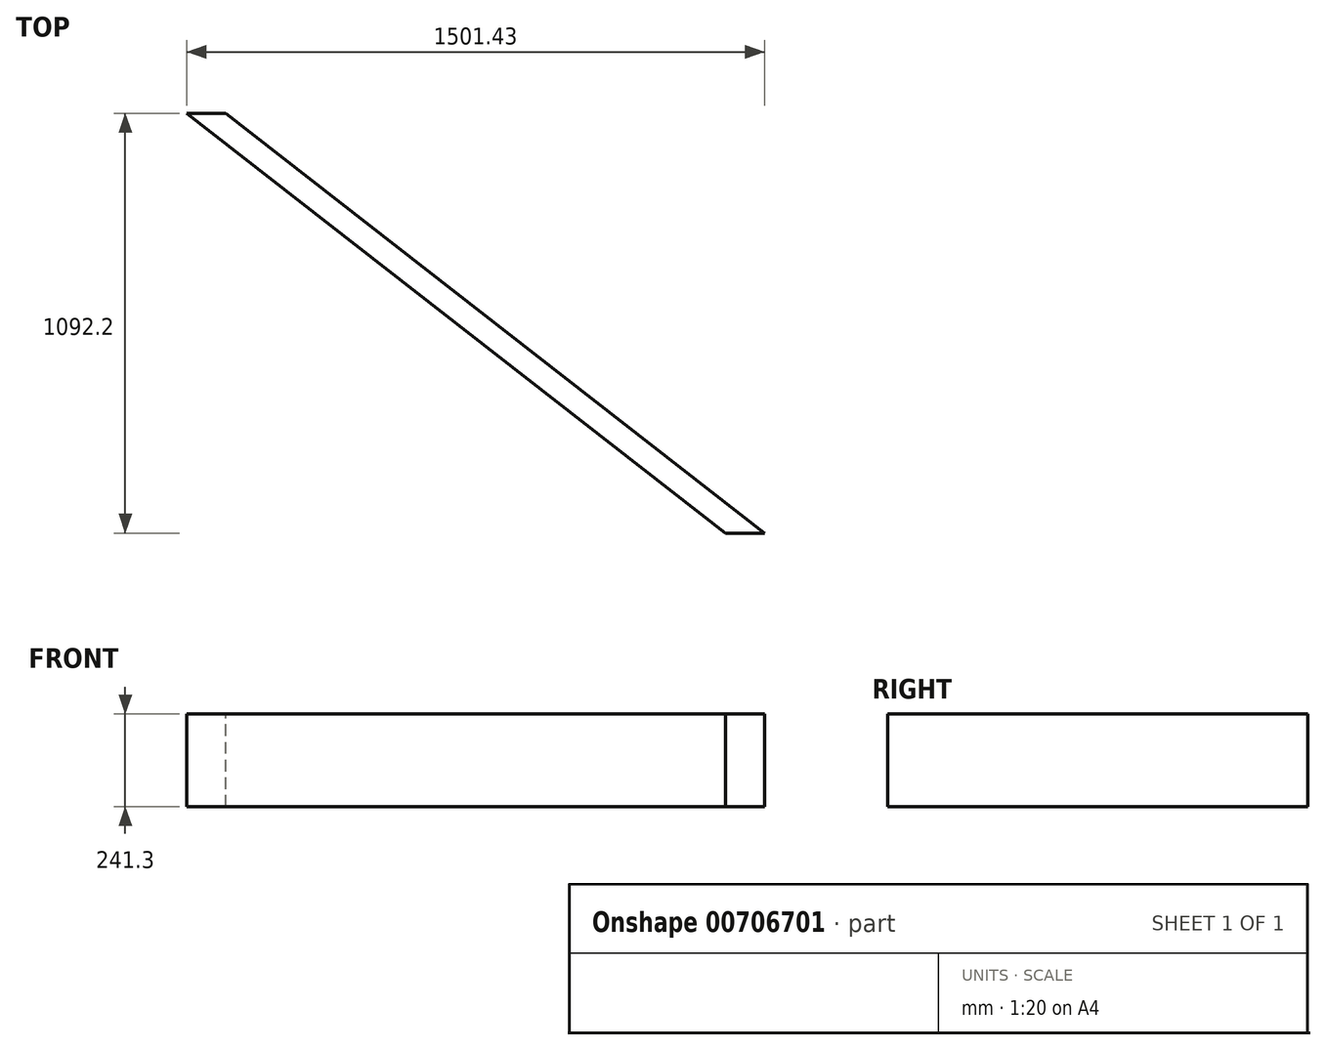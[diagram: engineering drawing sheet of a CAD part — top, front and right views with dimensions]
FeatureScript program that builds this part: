
annotation { "Feature Type Name" : "Feature", "Feature Type Description" : "" }
export const myFeature = defineFeature(function(context is Context, id is Id, definition is map)
    precondition{}
    {
        {
            var Q0;
            Q0=qCreatedBy(makeId("Top.planeOp"),FACE);
            var sketch = newSketch(context, id + "F0", { "sketchPlane" : qUnion([Q0])});
            skLineSegment(sketch, "E0", {"start": v(0, 0) * mm, "end": v(1399.83, -1092.2) * mm});
            skLineSegment(sketch, "E1", {"start": v(1399.83, -1092.2) * mm, "end": v(1501.43, -1092.2) * mm});
            skLineSegment(sketch, "E2", {"start": v(1501.43, -1092.2) * mm, "end": v(1501.43, 0) * mm});
            skLineSegment(sketch, "E3", {"start": v(1501.43, 0) * mm, "end": v(0, 0) * mm});
            skSolve(sketch);
        }
        {
            var Q0;
            Q0=makeQuery(id+"F0.imprint","IMPRINT",FACE,{"disambiguationData":[TD([[makeQuery(id+"F0.imprint","IMPRINT",EDGE,{"derivedFrom":sQuery(id+"F0.wireOp",EDGE,"E0")}),1.0]])]});
            extrude(context, id + "F1", {"entities" : qUnion([Q0]), "depth" : 241.3 * mm, "offsetDistance" : 25.4 * mm});
        }
        {
            var Q0;
            Q0=makeQuery(id+"F1.opExtrude","CAP_FACE",FACE,{"disambiguationData":[OSD([sQuery(id+"F0.wireOp",EDGE,"E0"),sQuery(id+"F0.wireOp",EDGE,"E1"),sQuery(id+"F0.wireOp",EDGE,"E2"),sQuery(id+"F0.wireOp",EDGE,"E3")])],"isStart":false});
            var sketch = newSketch(context, id + "F2", { "sketchPlane" : qUnion([Q0])});
            skLineSegment(sketch, "E4", {"start": v(1501.43, 0) * mm, "end": v(1501.43, -1092.2) * mm});
            skLineSegment(sketch, "E5", {"start": v(1501.43, -1092.2) * mm, "end": v(101.6, 0) * mm});
            skLineSegment(sketch, "E6", {"start": v(101.6, 0) * mm, "end": v(1501.43, 0) * mm});
            skSolve(sketch);
        }
        {
            var Q0;
            Q0=makeQuery(id+"F2.imprint","IMPRINT",FACE,{"disambiguationData":[TD([[makeQuery(id+"F2.imprint","IMPRINT",EDGE,{"derivedFrom":sQuery(id+"F2.wireOp",EDGE,"E4")}),1.0]])]});
            extrude(context, id + "F3", {"entities" : qUnion([Q0]), "operationType" : NewBodyOperationType.REMOVE, "oppositeDirection" : true, "depth" : 241.3 * mm, "offsetDistance" : 25.4 * mm});
        }
        {
            var Q0;
            Q0=makeQuery(id+"F1.opExtrude","SWEPT_FACE",FACE,{"disambiguationData":[OSD([sQuery(id+"F0.wireOp",EDGE,"E0")])]});
            var sketch = newSketch(context, id + "F4", { "sketchPlane" : qUnion([Q0])});
            skLineSegment(sketch, "E7.bottom", {"start": v(0, 0) * mm, "end": v(762, 0) * mm});
            skLineSegment(sketch, "E7.top", {"start": v(0, 50.8) * mm, "end": v(762, 50.8) * mm});
            skLineSegment(sketch, "E7.left", {"start": v(0, 0) * mm, "end": v(0, 50.8) * mm});
            skLineSegment(sketch, "E7.right", {"start": v(762, 0) * mm, "end": v(762, 50.8) * mm});
            skSolve(sketch);
        }
        {
            var Q0;
            {var subQ4=sQuery(id+"F4.wireOp",EDGE,"E7.top");Q0=makeQuery(id+"F4.imprint","IMPRINT",FACE,{"disambiguationData":[TD([[makeQuery(id+"F4.imprint","IMPRINT",EDGE,{"derivedFrom":subQ4}),1.0]])]});}
            var sketch = newSketch(context, id + "F5", { "sketchPlane" : qUnion([Q0])});
            skLineSegment(sketch, "E8.bottom", {"start": v(0, 0) * mm, "end": v(25.4, 0) * mm});
            skLineSegment(sketch, "E8.top", {"start": v(0, 50.8) * mm, "end": v(25.4, 50.8) * mm});
            skLineSegment(sketch, "E8.left", {"start": v(0, 0) * mm, "end": v(0, 50.8) * mm});
            skLineSegment(sketch, "E8.right", {"start": v(25.4, 0) * mm, "end": v(25.4, 50.8) * mm});
            skSolve(sketch);
        }
    });
